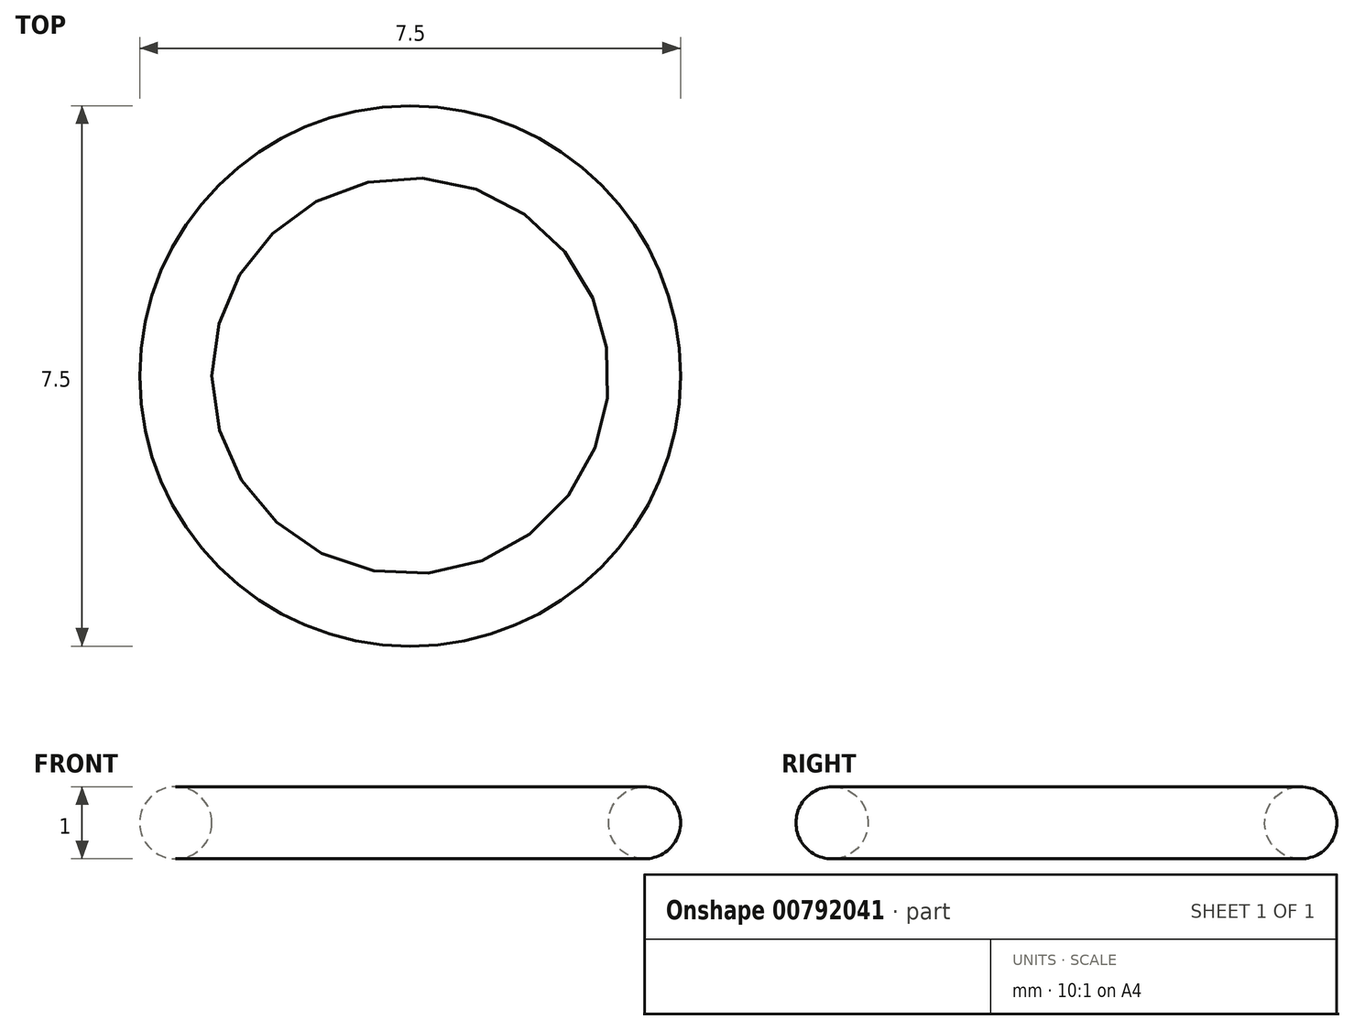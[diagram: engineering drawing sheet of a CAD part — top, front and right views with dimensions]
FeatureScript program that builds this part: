
annotation { "Feature Type Name" : "Feature", "Feature Type Description" : "" }
export const myFeature = defineFeature(function(context is Context, id is Id, definition is map)
    precondition{}
    {
        {
            var Q0;
            Q0=qCreatedBy(makeId("Front.planeOp"),FACE);
            var sketch = newSketch(context, id + "F0", { "sketchPlane" : qUnion([Q0])});
            skLineSegment(sketch, "E0", {"start": v(0, 0) * mm, "end": v(3.25, 0) * mm, "construction": true});
            skCircle(sketch, "E1", {"center": v(3.25, 0) * mm, "radius": 0.5 * mm});
            skLineSegment(sketch, "E2", {"start": v(0, 0) * mm, "end": v(0, 2.63) * mm, "construction": true});
            skLineSegment(sketch, "E3", {"start": v(0, 2.63) * mm, "end": v(0, 1.31) * mm, "construction": true});
            skLineSegment(sketch, "E4.0", {"start": v(3, 0) * mm, "end": v(3, 2.63) * mm});
            skSolve(sketch);
        }
        {
            var Q0;
            Q0 = qSketchRegion(id + "F0", true);
            var Q1;
            Q1=sQuery(id+"F0.wireOp",EDGE,"E2");
            revolve(context, id + "F1", {"surfaceOperationType" : NewSurfaceOperationType.NEW, "entities" : qUnion([Q0]), "axis" : qUnion([Q1]), "revolveType" : RevolveType.FULL});
        }
    });
